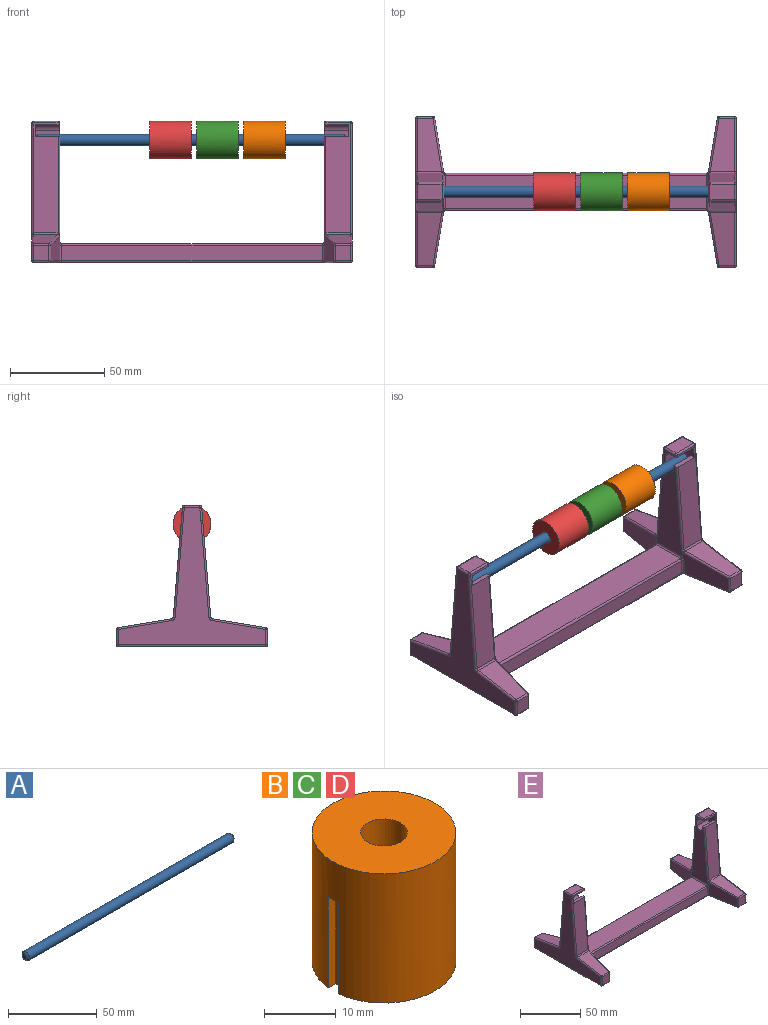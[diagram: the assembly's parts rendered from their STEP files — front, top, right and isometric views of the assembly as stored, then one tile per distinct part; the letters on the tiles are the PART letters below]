
ASSEMBLY  parts=5 mates=2
PART A: 5 faces, bbox 165x6x6 mm
  f0: cylinder r=3mm len=163mm, axis (-1,0,0), area 3072.5mm2, adj f3,f4
  f1: plane 4x4mm, normal (1,0,0), area 12.6mm2, adj f4
  f2: plane 4x4mm, normal (-1,0,0), area 12.6mm2, adj f3
  f3: cone r=3mm half-angle=45deg, axis (1,0,0), area 22.2mm2, adj f0,f2
  f4: cone r=2mm half-angle=45deg, axis (-1,0,0), area 22.2mm2, adj f0,f1
PART B: 8 faces, bbox 20x20x22 mm
  f0: plane 20x19.95mm, normal (0,0,-1), area 278mm2, adj f1,f2,f4,f5,f6
  f1: cylinder r=3.25mm len=22mm, axis (0,0,-1), area 449.2mm2, adj f0,f3
  f2: cylinder r=10mm len=22mm, axis (0,0,-1), area 1351.2mm2, adj f0,f3,f5,f6,f7
  f3: plane 20x20mm, normal (0,0,1), area 281mm2, adj f1,f2
  f4: plane 15.5x2mm, normal (-1,0,0), area 31mm2, adj f0,f5,f6,f7
  f5: plane 15.5x1.45mm, normal (0,-1,0), area 22.5mm2, adj f0,f2,f4,f7
  f6: plane 15.5x1.45mm, normal (0,1,0), area 22.5mm2, adj f0,f2,f4,f7
  f7: plane 2x1.5mm, normal (0,0,-1), area 3mm2, adj f2,f4,f5,f6
PART C: same geometry as B
PART D: same geometry as B
PART E: 154 faces, bbox 170x80x75 mm
  f0: plane 13x0.98mm, normal (0,-1,0.08), area 12.8mm2, adj f28,f40,f135,f146,f151
  f1: plane 13x8.16mm, normal (0,0,1), area 106.1mm2, adj f45,f46,f47,f48
  f2: plane 138.31x8mm, normal (0,1,0), area 1106.4mm2, adj f87,f88,f100,f101
  f3: plane 138.31x8mm, normal (0,-1,0), area 1106.4mm2, adj f97,f98,f105,f106
  f4: plane 58.31x13mm, normal (0,-1,0.08), area 686mm2, adj f37,f38,f39,f42,f47,f54,f58,f63
  f5: plane 51.13x13.01mm, normal (0,-1,0.08), area 666.9mm2, adj f27,f40,f136,f147,f152
  f6: plane 58.31x13mm, normal (0,1,0.08), area 760.6mm2, adj f45,f49,f53,f56
  f7: plane 58.31x13mm, normal (0,1,0.08), area 760.6mm2, adj f123,f124,f132,f133
  f8: plane 78x73mm, normal (1,0,0), area 1663.7mm2, adj f48,f49,f52,f54,f55,f59,f64,f65
  f9: plane 13x8.16mm, normal (0,0,1), area 106.1mm2, adj f133,f134,f145,f146
  f10: plane 29.19x13.17mm, normal (0.99,-0.16,0), area 305.2mm2, adj f26,f96,f102,f105,f114,f125,f137,f142
  f11: plane 29.19x13.17mm, normal (-0.99,-0.16,0), area 305.2mm2, adj f25,f62,f68,f72,f84,f91,f92,f98
  f12: plane 8.15x8.15mm, normal (0,-1,0), area 66.5mm2, adj f125,f126,f138,f139
  f13: plane 8.15x8.15mm, normal (0,1,0), area 66.5mm2, adj f108,f112,f115,f116
  f14: plane 168x78mm, normal (0,0,-1), area 4304.7mm2, adj f75,f76,f85,f86,f94,f99,f100,f103
  f15: plane 78x73mm, normal (-1,0,0), area 1663.9mm2, adj f116,f122,f127,f128,f132,f139,f145,f148
  f16: plane 8.15x8.15mm, normal (0,-1,0), area 66.5mm2, adj f73,f74,f84,f85
  f17: plane 8.15x8.15mm, normal (0,1,0), area 66.5mm2, adj f65,f66,f76,f77
  f18: plane 29.19x13.17mm, normal (0.99,0.16,0), area 305.2mm2, adj f26,f89,f95,f101,f107,f108,f113,f118
  f19: plane 29.19x13.17mm, normal (-0.99,0.16,0), area 305.2mm2, adj f25,f57,f61,f67,f77,f81,f82,f86
  f20: plane 28.4x12.89mm, normal (0,-0.16,0.99), area 302.8mm2, adj f63,f64,f72,f73
  f21: plane 28.4x12.89mm, normal (0,-0.16,0.99), area 302.8mm2, adj f137,f138,f147,f148
  f22: plane 28.4x12.89mm, normal (0,0.16,0.99), area 302.8mm2, adj f55,f56,f66,f67
  f23: plane 28.4x12.89mm, normal (0,0.16,0.99), area 302.8mm2, adj f112,f113,f122,f123
  f24: plane 138x18mm, normal (0,0,1), area 2484mm2, adj f83,f88,f90,f97
  f25: plane 63.27x20mm, normal (-1,0,0), area 779.4mm2, adj f11,f19,f33,f34,f35,f36,f37,f38
  f26: plane 63.27x20mm, normal (1,0,0), area 779.4mm2, adj f10,f18,f27,f28,f29,f30,f31,f32
  f27: plane 13.04x2.61mm, normal (0,0,1), area 33.3mm2, adj f5,f26,f32,f41,f136
  f28: plane 13.04x5.19mm, normal (0,0,-1), area 66.8mm2, adj f0,f26,f29,f41,f135
  f29: cylinder r=3.1mm len=13mm, axis (-1,0,0), area 63.3mm2, adj f26,f28,f30,f41
  f30: plane 13x5mm, normal (0,-1,0), area 65mm2, adj f26,f29,f31,f41
  f31: cylinder r=3.1mm len=13mm, axis (-1,0,0), area 126.6mm2, adj f26,f30,f32,f41
  f32: plane 13x1.9mm, normal (0,1,0), area 24.7mm2, adj f26,f27,f31,f41
  f33: plane 13x1.9mm, normal (0,1,0), area 24.7mm2, adj f25,f34,f38,f39
  f34: cylinder r=3.1mm len=13mm, axis (-1,0,0), area 126.6mm2, adj f25,f33,f35,f39
  f35: plane 13x5mm, normal (0,-1,0), area 65mm2, adj f25,f34,f36,f39
  f36: cylinder r=3.1mm len=13mm, axis (-1,0,0), area 63.3mm2, adj f25,f35,f37,f39
  f37: plane 13.04x5.19mm, normal (0,0,-1), area 66.8mm2, adj f4,f25,f36,f39,f42
  f38: plane 13.04x2.61mm, normal (0,0,1), area 33.3mm2, adj f4,f25,f33,f39,f58
  f39: plane 11.2x8.78mm, normal (-1,0,0), area 77.6mm2, adj f4,f33,f34,f35,f36,f37,f38
  f40: plane 6.21x1.01mm, normal (0,-1,0.08), area 6.2mm2, adj f0,f5,f41,f153
  f41: plane 11.2x8.78mm, normal (1,0,0), area 77.6mm2, adj f27,f28,f29,f30,f31,f32,f40
  f42: cylinder r=1mm len=1.08mm, axis (0,-0.08,-1), area 1.5mm2, adj f4,f25,f37,f43
  f43: sphere r=1mm, area 1.5mm2, adj f42,f46,f47
  f44: sphere r=1mm, area 1mm2, adj f45,f48,f49
  f45: cylinder r=1mm len=13mm, axis (-1,0,0), area 19.3mm2, adj f1,f6,f44,f50
  f46: cylinder r=1mm len=8.16mm, axis (0,-1,0), area 12.8mm2, adj f1,f25,f43,f50
  f47: cylinder r=1mm len=13mm, axis (1,0,0), area 19.3mm2, adj f1,f4,f43,f51
  f48: cylinder r=1mm len=8.16mm, axis (0,-1,0), area 12.8mm2, adj f1,f8,f44,f51
  f49: cylinder r=1mm len=58.39mm, axis (0,-0.08,1), area 91.9mm2, adj f6,f8,f44,f52
  f50: sphere r=1mm, area 2mm2, adj f45,f46,f53
  f51: sphere r=1mm, area 1.5mm2, adj f47,f48,f54
  f52: torus R=2mm, axis (-1,0,0), area 2.8mm2, adj f8,f49,f55,f56
  f53: cylinder r=1mm len=58.39mm, axis (0,-0.08,1), area 91.9mm2, adj f6,f25,f50,f57
  f54: cylinder r=1mm len=58.39mm, axis (0,-0.08,-1), area 91.9mm2, adj f4,f8,f51,f59
  f55: cylinder r=1mm len=28.56mm, axis (0,-0.99,0.16), area 45.2mm2, adj f8,f22,f52,f60
  f56: cylinder r=1mm len=13mm, axis (-1,0,0), area 17.2mm2, adj f6,f22,f52,f57,f61
  f57: torus R=2mm, axis (-1,0,0), area 2.1mm2, adj f19,f25,f53,f56,f61
  f58: cylinder r=1mm len=51.29mm, axis (0,-0.08,-1), area 80.7mm2, adj f4,f25,f38,f62
  f59: torus R=2mm, axis (-1,0,0), area 2.8mm2, adj f8,f54,f63,f64
  f60: sphere r=1mm, area 0.9mm2, adj f55,f65,f66
  f61: bspline ~1.13x1.11mm, area 0.8mm2, adj f19,f56,f57,f67
  f62: torus R=2mm, axis (-1,0,0), area 2.1mm2, adj f11,f25,f58,f63,f68
  f63: cylinder r=1mm len=13mm, axis (-1,0,0), area 17.2mm2, adj f4,f20,f59,f62,f68
  f64: cylinder r=1mm len=28.56mm, axis (0,-0.99,-0.16), area 45.2mm2, adj f8,f20,f59,f69
  f65: cylinder r=1mm len=8.15mm, axis (0,0,1), area 12.8mm2, adj f8,f17,f60,f70
  f66: cylinder r=1mm len=8.15mm, axis (1,0,0), area 11.5mm2, adj f17,f22,f60,f71
  f67: cylinder r=1mm len=28.46mm, axis (0.16,0.97,-0.16), area 45mm2, adj f19,f22,f61,f71
  f68: bspline ~1.13x1.11mm, area 0.8mm2, adj f11,f62,f63,f72
  f69: sphere r=1mm, area 0.9mm2, adj f64,f73,f74
  f70: sphere r=1mm, area 1mm2, adj f65,f75,f76
  f71: sphere r=1mm, area 0.8mm2, adj f66,f67,f77
  f72: cylinder r=1mm len=28.46mm, axis (-0.16,0.97,0.16), area 45mm2, adj f11,f20,f68,f78
  f73: cylinder r=1mm len=8.15mm, axis (1,0,0), area 11.5mm2, adj f16,f20,f69,f78
  f74: cylinder r=1mm len=8.15mm, axis (0,0,-1), area 12.8mm2, adj f8,f16,f69,f79
  f75: cylinder r=1mm len=78mm, axis (0,1,0), area 122.5mm2, adj f8,f14,f70,f79
  f76: cylinder r=1mm len=8.15mm, axis (-1,0,0), area 12.8mm2, adj f14,f17,f70,f80
  f77: cylinder r=1mm len=8.15mm, axis (0,0,-1), area 11.5mm2, adj f17,f19,f71,f80
  f78: sphere r=1mm, area 0.8mm2, adj f72,f73,f84
  f79: sphere r=1mm, area 1.6mm2, adj f74,f75,f85
  f80: sphere r=1mm, area 2mm2, adj f76,f77,f86
  f81: bspline ~1.68x1.31mm, area 1.9mm2, adj f19,f82,f87,f88
  f82: torus R=2mm, axis (-1,0,0), area 1.2mm2, adj f19,f25,f81,f83,f88
  f83: cylinder r=1mm len=18mm, axis (0,1,0), area 28.3mm2, adj f24,f25,f82,f91
  f84: cylinder r=1mm len=8.15mm, axis (0,0,-1), area 11.5mm2, adj f11,f16,f78,f93
  f85: cylinder r=1mm len=8.15mm, axis (1,0,0), area 12.8mm2, adj f14,f16,f79,f93
  f86: cylinder r=1mm len=28.49mm, axis (-0.16,-0.99,0), area 45.1mm2, adj f14,f19,f80,f94
  f87: cylinder r=1mm len=8mm, axis (0,0,-1), area 11.2mm2, adj f2,f19,f81,f94
  f88: cylinder r=1mm len=138.31mm, axis (1,0,0), area 216.9mm2, adj f2,f24,f81,f82,f89,f95
  f89: torus R=2mm, axis (1,0,0), area 1.2mm2, adj f18,f26,f88,f90,f95
  f90: cylinder r=1mm len=18mm, axis (0,1,0), area 28.3mm2, adj f24,f26,f89,f96
  f91: torus R=2mm, axis (-1,0,0), area 1.2mm2, adj f11,f25,f83,f92,f97
  f92: bspline ~1.68x1.31mm, area 1.9mm2, adj f11,f91,f97,f98
  f93: sphere r=1mm, area 0.9mm2, adj f84,f85,f99
  f94: torus R=2mm, axis (0,0,1), area 3mm2, adj f14,f86,f87,f100
  f95: bspline ~1.68x1.31mm, area 1.9mm2, adj f18,f88,f89,f101
  f96: torus R=2mm, axis (1,0,0), area 1.2mm2, adj f10,f26,f90,f97,f102
  f97: cylinder r=1mm len=138.31mm, axis (-1,0,0), area 216.9mm2, adj f3,f24,f91,f92,f96,f102
  f98: cylinder r=1mm len=8mm, axis (0,0,1), area 11.2mm2, adj f3,f11,f92,f103
  f99: cylinder r=1mm len=28.49mm, axis (0.16,-0.99,0), area 45.1mm2, adj f11,f14,f93,f103
  f100: cylinder r=1mm len=138.31mm, axis (-1,0,0), area 217.3mm2, adj f2,f14,f94,f104
  f101: cylinder r=1mm len=8mm, axis (0,0,1), area 11.2mm2, adj f2,f18,f95,f104
  f102: bspline ~1.68x1.31mm, area 1.9mm2, adj f10,f96,f97,f105
  f103: torus R=2mm, axis (0,0,1), area 3mm2, adj f14,f98,f99,f106
  f104: torus R=2mm, axis (0,0,1), area 3mm2, adj f14,f100,f101,f107
  f105: cylinder r=1mm len=8mm, axis (0,0,1), area 11.2mm2, adj f3,f10,f102,f110
  f106: cylinder r=1mm len=138.31mm, axis (1,0,0), area 217.3mm2, adj f3,f14,f103,f110
  f107: cylinder r=1mm len=28.49mm, axis (-0.16,0.99,0), area 45.1mm2, adj f14,f18,f104,f111
  f108: cylinder r=1mm len=8.15mm, axis (0,0,1), area 11.5mm2, adj f13,f18,f109,f111
  f109: sphere r=1mm, area 0.8mm2, adj f108,f112,f113
  f110: torus R=2mm, axis (0,0,1), area 3mm2, adj f14,f105,f106,f114
  f111: sphere r=1mm, area 0.9mm2, adj f107,f108,f115
  f112: cylinder r=1mm len=8.15mm, axis (1,0,0), area 11.5mm2, adj f13,f23,f109,f117
  f113: cylinder r=1mm len=28.46mm, axis (0.16,-0.97,0.16), area 45mm2, adj f18,f23,f109,f118
  f114: cylinder r=1mm len=28.49mm, axis (0.16,0.99,0), area 45.1mm2, adj f10,f14,f110,f120
  f115: cylinder r=1mm len=8.15mm, axis (-1,0,0), area 12.8mm2, adj f13,f14,f111,f121
  f116: cylinder r=1mm len=8.15mm, axis (0,0,-1), area 12.8mm2, adj f13,f15,f117,f121
  f117: sphere r=1mm, area 0.9mm2, adj f112,f116,f122
  f118: bspline ~1.13x1.11mm, area 0.8mm2, adj f18,f113,f119,f123
  f119: torus R=2mm, axis (1,0,0), area 2.1mm2, adj f18,f26,f118,f123,f124
  f120: sphere r=1mm, area 1.4mm2, adj f114,f125,f126
  f121: sphere r=1mm, area 2.1mm2, adj f115,f116,f127
  f122: cylinder r=1mm len=28.56mm, axis (0,0.99,-0.16), area 45.2mm2, adj f15,f23,f117,f128
  f123: cylinder r=1mm len=13mm, axis (-1,0,0), area 17.2mm2, adj f7,f23,f118,f119,f128
  f124: cylinder r=1mm len=58.39mm, axis (0,0.08,-1), area 91.9mm2, adj f7,f26,f119,f129
  f125: cylinder r=1mm len=8.15mm, axis (0,0,-1), area 11.5mm2, adj f10,f12,f120,f130
  f126: cylinder r=1mm len=8.15mm, axis (1,0,0), area 12.8mm2, adj f12,f14,f120,f131
  f127: cylinder r=1mm len=78mm, axis (0,-1,0), area 122.5mm2, adj f14,f15,f121,f131
  f128: torus R=2mm, axis (-1,0,0), area 2.8mm2, adj f15,f122,f123,f132
  f129: sphere r=1mm, area 1mm2, adj f124,f133,f134
  f130: sphere r=1mm, area 0.8mm2, adj f125,f137,f138
  f131: sphere r=1mm, area 1.6mm2, adj f126,f127,f139
  f132: cylinder r=1mm len=58.39mm, axis (0,0.08,-1), area 91.9mm2, adj f7,f15,f128,f140
  f133: cylinder r=1mm len=13mm, axis (-1,0,0), area 19.3mm2, adj f7,f9,f129,f140
  f134: cylinder r=1mm len=8.16mm, axis (0,-1,0), area 12.8mm2, adj f9,f26,f129,f141
  f135: cylinder r=1mm len=1.08mm, axis (0,0.08,1), area 1.5mm2, adj f0,f26,f28,f141
  f136: cylinder r=1mm len=51.29mm, axis (0,0.08,1), area 80.7mm2, adj f5,f26,f27,f142
  f137: cylinder r=1mm len=28.46mm, axis (-0.16,-0.97,-0.16), area 45mm2, adj f10,f21,f130,f143
  f138: cylinder r=1mm len=8.15mm, axis (1,0,0), area 11.5mm2, adj f12,f21,f130,f144
  f139: cylinder r=1mm len=8.15mm, axis (0,0,1), area 12.8mm2, adj f12,f15,f131,f144
  f140: sphere r=1mm, area 1.5mm2, adj f132,f133,f145
  f141: sphere r=1mm, area 1.5mm2, adj f134,f135,f146
  f142: torus R=2mm, axis (1,0,0), area 2.1mm2, adj f10,f26,f136,f143,f147
  f143: bspline ~1.13x1.11mm, area 0.8mm2, adj f10,f137,f142,f147
  f144: sphere r=1mm, area 0.9mm2, adj f138,f139,f148
  f145: cylinder r=1mm len=8.16mm, axis (0,1,0), area 12.8mm2, adj f9,f15,f140,f149
  f146: cylinder r=1mm len=13mm, axis (1,0,0), area 19.3mm2, adj f0,f9,f141,f149
  f147: cylinder r=1mm len=13mm, axis (-1,0,0), area 17.2mm2, adj f5,f21,f142,f143,f150
  f148: cylinder r=1mm len=28.56mm, axis (0,0.99,0.16), area 45.2mm2, adj f15,f21,f144,f150
  f149: sphere r=1mm, area 1mm2, adj f145,f146,f151
  f150: torus R=2mm, axis (-1,0,0), area 2.8mm2, adj f15,f147,f148,f152
  f151: cylinder r=1mm len=1.08mm, axis (0,0.08,1), area 1.5mm2, adj f0,f15,f149,f153
  f152: cylinder r=1mm len=51.21mm, axis (0,0.08,1), area 80.6mm2, adj f5,f15,f150,f153
  f153: cylinder r=1mm len=6.28mm, axis (0,0.08,1), area 9.8mm2, adj f15,f40,f151,f152
PLACE A t=(-53.6,121.77,104.49)mm
PLACE B rot(axis=(0,-1,0),90deg) t=(78.9,121.77,104.49)mm
PLACE C rot(axis=(0,-1,0),90deg) t=(53.9,121.77,104.49)mm
PLACE D rot(axis=(0,-1,0),90deg) t=(28.9,121.77,104.49)mm
PLACE E t=(-55.6,81.77,39.49)mm
MATE revolute D.f2 <-> A.f0  axis (1,0,0) through (28.9,121.77,104.49)mm
MATE revolute E.f31 <-> A.f0  axis (1,0,0) through (-53.6,121.77,104.49)mm
